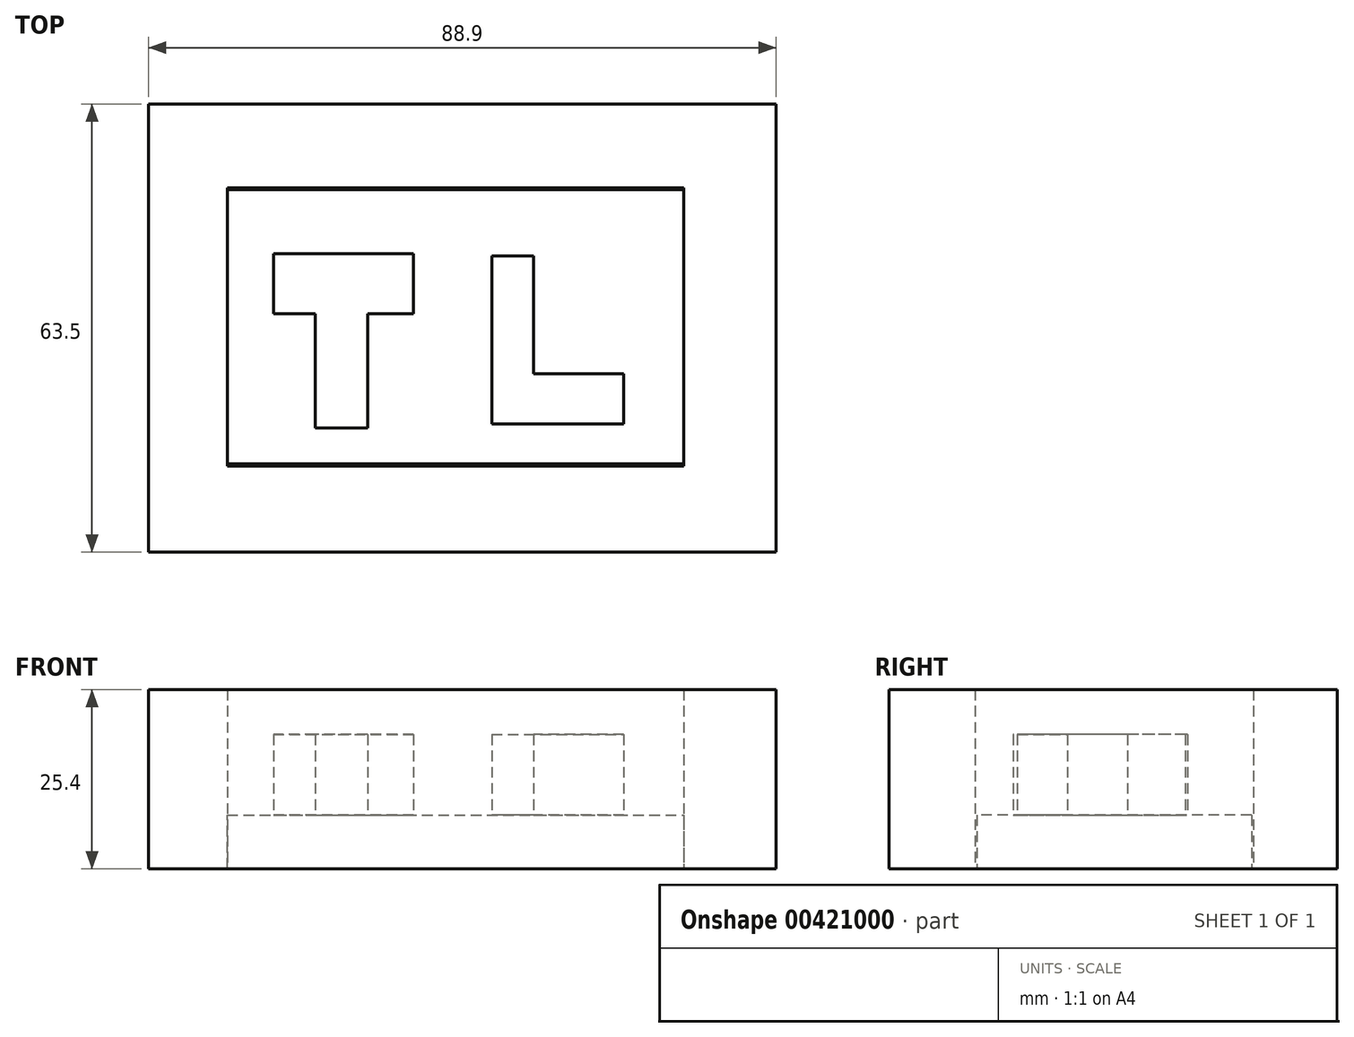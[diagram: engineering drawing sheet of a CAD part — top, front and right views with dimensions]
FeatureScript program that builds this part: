
annotation { "Feature Type Name" : "Feature", "Feature Type Description" : "" }
export const myFeature = defineFeature(function(context is Context, id is Id, definition is map)
    precondition{}
    {
        {
            var Q0;
            Q0=qCreatedBy(makeId("Top.planeOp"),FACE);
            var sketch = newSketch(context, id + "F0", { "sketchPlane" : qUnion([Q0])});
            skLineSegment(sketch, "E0.bottom", {"start": v(-52.44, 32) * mm, "end": v(36.46, 32) * mm});
            skLineSegment(sketch, "E0.top", {"start": v(-52.44, -31.5) * mm, "end": v(36.46, -31.5) * mm});
            skLineSegment(sketch, "E0.left", {"start": v(-52.44, 32) * mm, "end": v(-52.44, -31.5) * mm});
            skLineSegment(sketch, "E0.right", {"start": v(36.46, 32) * mm, "end": v(36.46, -31.5) * mm});
            skLineSegment(sketch, "E1.bottom", {"start": v(-41.28, 20.14) * mm, "end": v(23.4, 20.14) * mm});
            skLineSegment(sketch, "E1.top", {"start": v(-41.28, -19.3) * mm, "end": v(23.4, -19.3) * mm});
            skLineSegment(sketch, "E1.left", {"start": v(-41.28, 20.14) * mm, "end": v(-41.28, -19.3) * mm});
            skLineSegment(sketch, "E1.right", {"start": v(23.4, 20.14) * mm, "end": v(23.4, -19.3) * mm});
            skSolve(sketch);
        }
        {
            var Q0;
            Q0=makeQuery(id+"F0.imprint","IMPRINT",FACE,{"disambiguationData":[TD([[makeQuery(id+"F0.imprint","IMPRINT",EDGE,{"derivedFrom":sQuery(id+"F0.wireOp",EDGE,"E0.bottom")}),-1.0]])]});
            extrude(context, id + "F1", {"entities" : qUnion([Q0]), "depth" : 25.4 * mm});
        }
        {
            var Q0;
            Q0=qCreatedBy(makeId("Top.planeOp"),FACE);
            var sketch = newSketch(context, id + "F2", { "sketchPlane" : qUnion([Q0])});
            skLineSegment(sketch, "E2.bottom", {"start": v(-41.57, 19.86) * mm, "end": v(23.4, 19.86) * mm});
            skLineSegment(sketch, "E2.top", {"start": v(-41.57, -19) * mm, "end": v(23.4, -19) * mm});
            skLineSegment(sketch, "E2.left", {"start": v(-41.57, 19.86) * mm, "end": v(-41.57, -19) * mm});
            skLineSegment(sketch, "E2.right", {"start": v(23.4, 19.86) * mm, "end": v(23.4, -19) * mm});
            skSolve(sketch);
        }
        {
            var Q0;
            Q0 = qSketchRegion(id + "F2", true);
            extrude(context, id + "F3", {"entities" : qUnion([Q0]), "operationType" : NewBodyOperationType.ADD, "depth" : 7.62 * mm});
        }
        {
            var Q0;
            Q0=qCreatedBy(makeId("Top.planeOp"),FACE);
            var sketch = newSketch(context, id + "F4", { "sketchPlane" : qUnion([Q0])});
            skLineSegment(sketch, "E3", {"start": v(-34.76, 10.78) * mm, "end": v(-14.9, 10.78) * mm});
            skLineSegment(sketch, "E4", {"start": v(-14.9, 2.27) * mm, "end": v(-21.42, 2.27) * mm});
            skLineSegment(sketch, "E5", {"start": v(-21.42, 2.27) * mm, "end": v(-21.42, -13.9) * mm});
            skLineSegment(sketch, "E6", {"start": v(-21.42, -13.9) * mm, "end": v(-28.8, -13.9) * mm});
            skLineSegment(sketch, "E7", {"start": v(-28.8, -13.9) * mm, "end": v(-28.8, 2.27) * mm});
            skLineSegment(sketch, "E8", {"start": v(-28.8, 2.27) * mm, "end": v(-34.76, 2.27) * mm});
            skLineSegment(sketch, "E9", {"start": v(-34.76, 10.78) * mm, "end": v(-34.76, 2.27) * mm});
            skLineSegment(sketch, "E10", {"start": v(-14.9, 10.78) * mm, "end": v(-14.9, 2.27) * mm});
            skSolve(sketch);
        }
        {
            var Q0;
            Q0 = qSketchRegion(id + "F4", true);
            extrude(context, id + "F5", {"entities" : qUnion([Q0]), "operationType" : NewBodyOperationType.ADD, "depth" : 19.05 * mm});
        }
        {
            var Q0;
            Q0=qCreatedBy(makeId("Top.planeOp"),FACE);
            var sketch = newSketch(context, id + "F6", { "sketchPlane" : qUnion([Q0])});
            skLineSegment(sketch, "E11", {"start": v(-3.83, 10.5) * mm, "end": v(-3.83, -13.34) * mm});
            skLineSegment(sketch, "E12", {"start": v(-3.83, -13.34) * mm, "end": v(14.9, -13.34) * mm});
            skLineSegment(sketch, "E13", {"start": v(14.9, -13.34) * mm, "end": v(14.9, -6.24) * mm});
            skLineSegment(sketch, "E14", {"start": v(14.9, -6.24) * mm, "end": v(2.13, -6.24) * mm});
            skLineSegment(sketch, "E15", {"start": v(-3.83, 10.5) * mm, "end": v(2.13, 10.5) * mm});
            skLineSegment(sketch, "E16", {"start": v(2.13, 10.5) * mm, "end": v(2.13, -6.24) * mm});
            skSolve(sketch);
        }
        {
            var Q0;
            Q0 = qSketchRegion(id + "F6", true);
            extrude(context, id + "F7", {"entities" : qUnion([Q0]), "operationType" : NewBodyOperationType.ADD, "depth" : 19.05 * mm});
        }
    });
